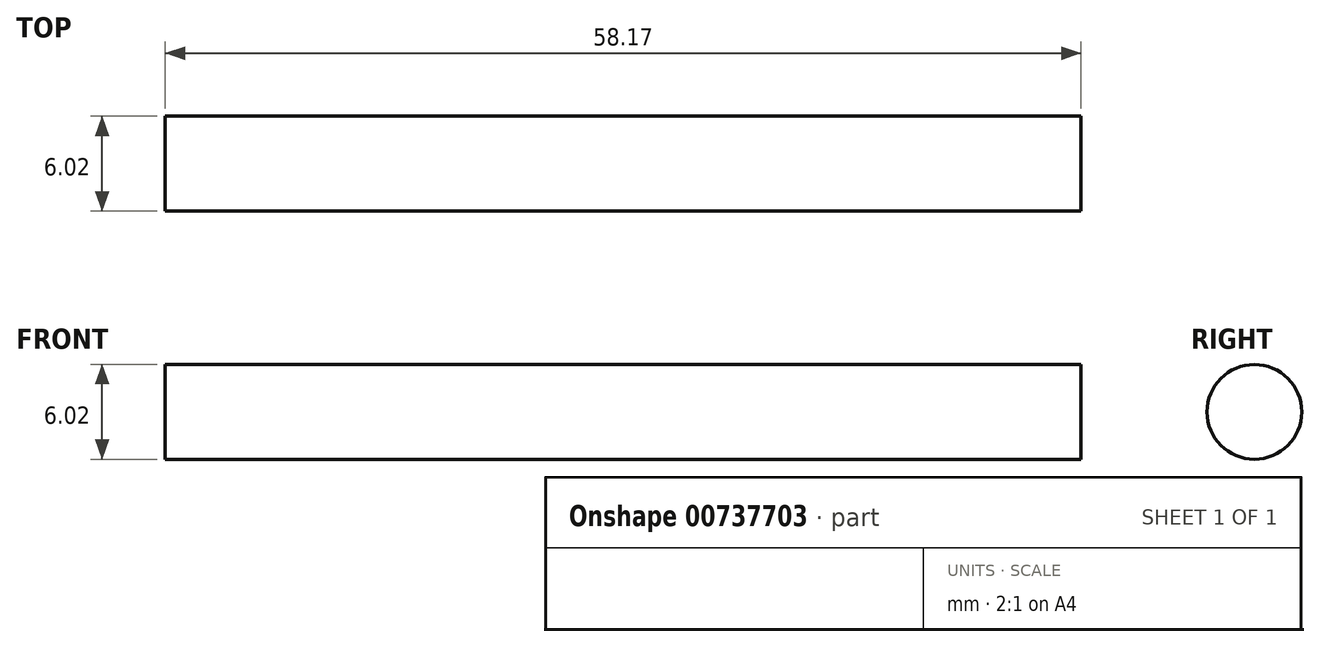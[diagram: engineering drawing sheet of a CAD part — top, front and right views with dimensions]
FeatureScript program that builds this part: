
annotation { "Feature Type Name" : "Feature", "Feature Type Description" : "" }
export const myFeature = defineFeature(function(context is Context, id is Id, definition is map)
    precondition{}
    {
        {
            var Q0;
            Q0=qCreatedBy(makeId("Right.planeOp"),FACE);
            var sketch = newSketch(context, id + "F0", { "sketchPlane" : qUnion([Q0])});
            skCircle(sketch, "E0", {"center": v(0, 0) * mm, "radius": 3.01 * mm});
            skSolve(sketch);
        }
        {
            var Q0;
            Q0=qSketchRegion(id+"F0",true);
            extrude(context, id + "F1", {"entities" : qUnion([Q0]), "depth" : 58.17 * mm, "offsetDistance" : 25.4 * mm});
        }
    });
